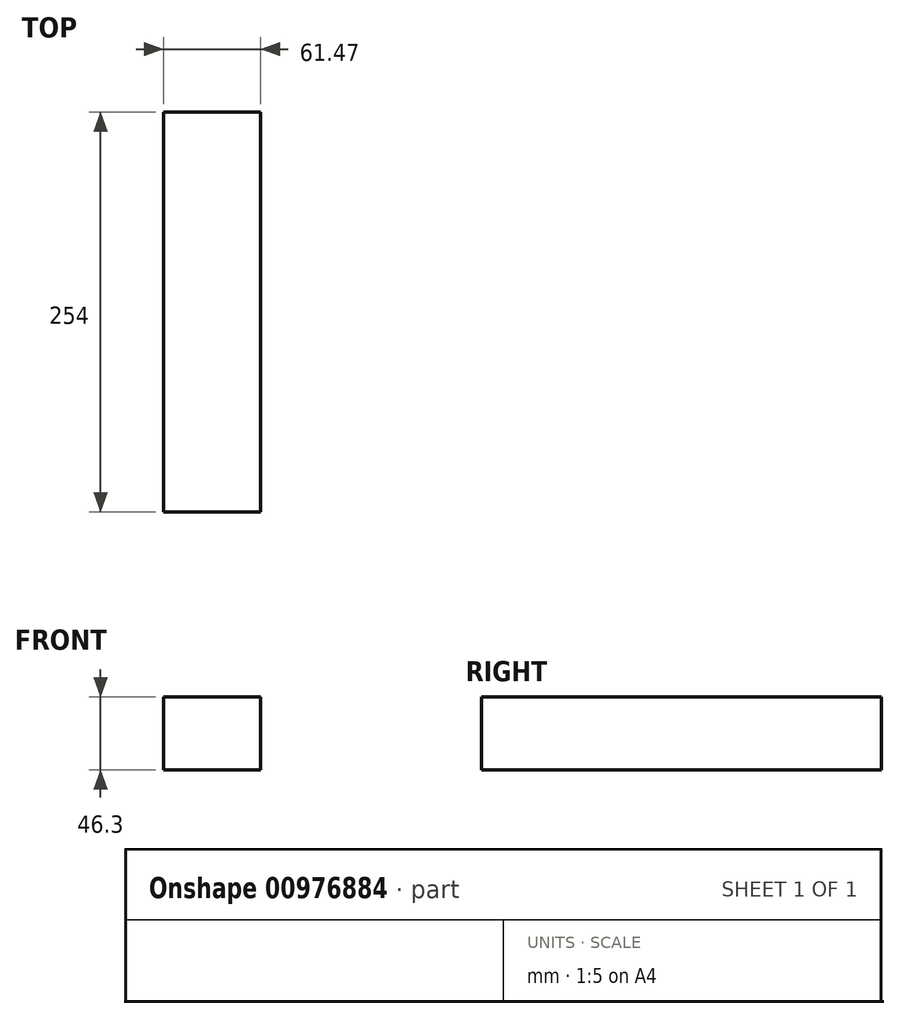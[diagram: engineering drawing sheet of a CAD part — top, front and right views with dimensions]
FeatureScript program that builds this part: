
annotation { "Feature Type Name" : "Feature", "Feature Type Description" : "" }
export const myFeature = defineFeature(function(context is Context, id is Id, definition is map)
    precondition{}
    {
        {
            var Q0;
            Q0=qCreatedBy(makeId("Front.planeOp"),FACE);
            var sketch = newSketch(context, id + "F0", { "sketchPlane" : qUnion([Q0])});
            skLineSegment(sketch, "E0.bottom", {"start": v(-53.61, 50.29) * mm, "end": v(7.86, 50.29) * mm});
            skLineSegment(sketch, "E0.top", {"start": v(-53.61, 3.99) * mm, "end": v(7.86, 3.99) * mm});
            skLineSegment(sketch, "E0.left", {"start": v(-53.61, 50.29) * mm, "end": v(-53.61, 3.99) * mm});
            skLineSegment(sketch, "E0.right", {"start": v(7.86, 50.29) * mm, "end": v(7.86, 3.99) * mm});
            skSolve(sketch);
        }
        {
            var Q0;
            Q0 = qSketchRegion(id + "F0", true);
            extrude(context, id + "F1", {"entities" : qUnion([Q0]), "depth" : 254 * mm, "offsetDistance" : 25.4 * mm});
        }
    });
